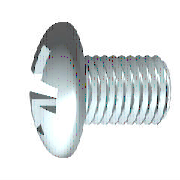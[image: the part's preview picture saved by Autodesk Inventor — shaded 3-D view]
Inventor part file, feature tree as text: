
AUTODESK INVENTOR PART (.ipt)
format: ipt  version: 2015 SP1 (Build 190203100, 203)  size: 260,096 bytes
history: native  units: mm (DEFAULTED — no unit token found)
features: extrude x1, other x1, plane x1
ambient origin geometry x7: Origin, YZ Plane, XZ Plane, X Axis, Y Axis, Z Axis, Center Point
bodies: Solid1 (feature_tree), Body (feature_tree)
feature tree (3):
  extrude  "Slot"  Depth=4.1656mm
  other  "Cut"
  plane  "Work Plane3"
